FCSTD DOCUMENT  (FreeCAD 0.20R28936 (Git))
Label: ScrewData
License: Creative Commons Attribution-NonCommercial-ShareAlike
LicenseURL: http://creativecommons.org/licenses/by-nc-sa/4.0/
objects: Spreadsheet::Sheet×1

FEATURE [Spreadsheet::Sheet] Spreadsheet001  label="Screws"
  cells = A2=Screw dimensions; B4=Name; C4=Value; D4=Description; B5=M3Radius; C5(M3Radius)==1.65mm; B6=M3HeadRadius; C6(M3HeadRadius)==3mm; B7=M3HeadHeight; C7(M3HeadHeight)==2.95mm; B8=M3WasherRadius; C8(M3WasherRadius)==3.7mm; B9=M3WasherHeight; C9(M3WasherHeight)==0.5mm; B10=M3NutRadius; C10(M3NutRadius)==3.4mm; B11=M3NutHeight; C11(M3NutHeight)==2.5mm; B12=M3NylocNutHeight; C12(M3NylocNutHeight)==4.1mm; B13=M3NutChannelWidth; C13(M3NutChannelWidth)==5.65mm; B14=M4Radius; C14(M4Radius)==2.2mm; B15=M4HeadRadius; C15(M4HeadRadius)==3.75mm; B16=M4HeadHeight; C16(M4HeadHeight)==4mm; B17=M4WasherRadius; C17(M4WasherRadius)==4.7mm; B18=M4NutRadius; C18(M4NutRadius)==4.25mm; B19=M4NutHeight; C19(M4NutHeight)==3.3mm; B20=M4NutDuctWidth; C20(M4NutDuctWidth)==7.1mm; B21=M5Radius; C21(M5Radius)==2.66mm; B22=M5HeadRadius; C22(M5HeadRadius)==4.5mm; B23=M5HeadHeight; C23(M5HeadHeight)==5mm; B24=M5NutRadius; C24(M5NutRadius)==4.75mm; B25=M5NutHeight; C25(M5NutHeight)==4mm; B27=M6Radius; C27(M6Radius)==3.15mm; B28=M6HeadRadius; C28(M6HeadRadius)==5.5mm; B35=0
